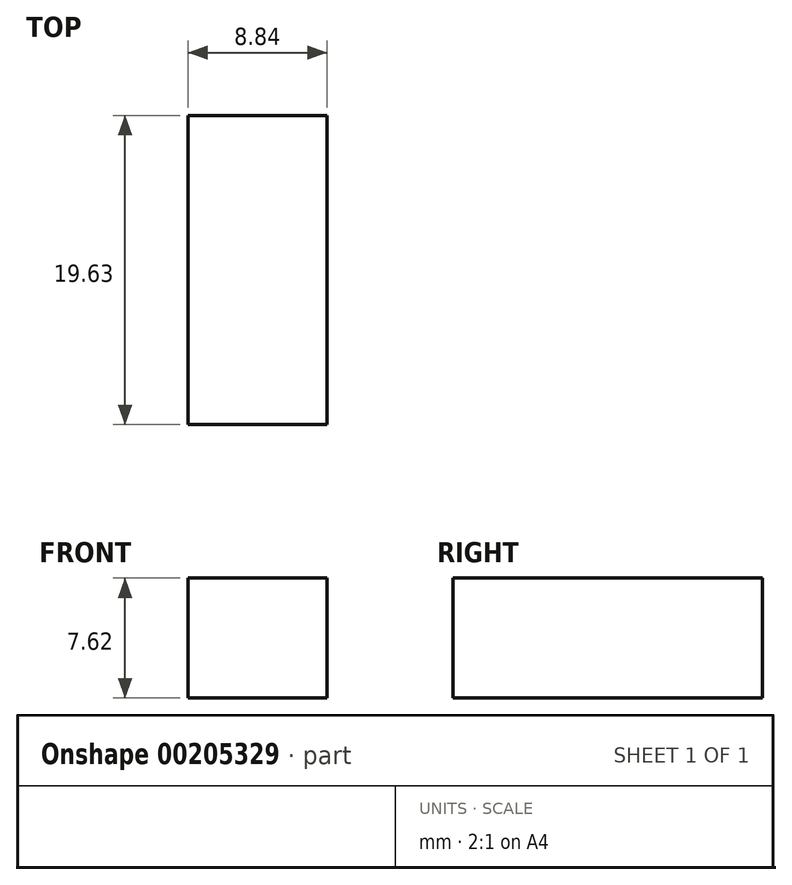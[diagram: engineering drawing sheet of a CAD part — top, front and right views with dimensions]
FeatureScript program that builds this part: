
annotation { "Feature Type Name" : "Feature", "Feature Type Description" : "" }
export const myFeature = defineFeature(function(context is Context, id is Id, definition is map)
    precondition{}
    {
        {
            var Q0;
            Q0=qCreatedBy(makeId("Top.planeOp"),FACE);
            var sketch = newSketch(context, id + "F0", { "sketchPlane" : qUnion([Q0])});
            skLineSegment(sketch, "E0.bottom", {"start": v(-60.42, 23.61) * mm, "end": v(52.56, 23.61) * mm});
            skLineSegment(sketch, "E0.top", {"start": v(-60.42, -27.19) * mm, "end": v(52.56, -27.19) * mm});
            skLineSegment(sketch, "E0.left", {"start": v(-60.42, 23.61) * mm, "end": v(-60.42, -27.19) * mm});
            skLineSegment(sketch, "E0.right", {"start": v(52.56, 23.61) * mm, "end": v(52.56, -27.19) * mm});
            skSolve(sketch);
        }
        {
            var Q0;
            Q0=makeQuery(id+"F0.imprint","IMPRINT",FACE,{"disambiguationData":[TD([[makeQuery(id+"F0.imprint","IMPRINT",EDGE,{"derivedFrom":sQuery(id+"F0.wireOp",EDGE,"E0.bottom")}),-1.0]])]});
            extrude(context, id + "F1", {"entities" : qUnion([Q0]), "oppositeDirection" : true, "depth" : 7.62 * mm});
        }
        {
            var Q0;
            Q0=makeQuery(id+"F1.opExtrude","CAP_FACE",FACE,{"disambiguationData":[OSD([sQuery(id+"F0.wireOp",EDGE,"E0.bottom"),sQuery(id+"F0.wireOp",EDGE,"E0.top"),sQuery(id+"F0.wireOp",EDGE,"E0.left"),sQuery(id+"F0.wireOp",EDGE,"E0.right")])],"isStart":true});
            var sketch = newSketch(context, id + "F2", { "sketchPlane" : qUnion([Q0])});
            skLineSegment(sketch, "E1.bottom", {"start": v(-4.56, -7.56) * mm, "end": v(4.28, -7.56) * mm});
            skLineSegment(sketch, "E1.top", {"start": v(-4.56, -27.19) * mm, "end": v(4.28, -27.19) * mm});
            skLineSegment(sketch, "E1.left", {"start": v(-4.56, -7.56) * mm, "end": v(-4.56, -27.19) * mm});
            skLineSegment(sketch, "E1.right", {"start": v(4.28, -7.56) * mm, "end": v(4.28, -27.19) * mm});
            skSolve(sketch);
        }
        {
            var Q0;
            Q0=makeQuery(id+"F2.imprint","IMPRINT",FACE,{"disambiguationData":[TD([[makeQuery(id+"F2.imprint","IMPRINT",EDGE,{"derivedFrom":sQuery(id+"F2.wireOp",EDGE,"E1.bottom")}),1.0]])]});
            var Q1;
            Q1=sQuery(id+"F2.wireOp",EDGE,"E1.top");
            var Q2;
            Q2=sQuery(id+"F2.wireOp",EDGE,"E1.left");
            var Q3;
            Q3=sQuery(id+"F2.wireOp",EDGE,"E1.bottom");
            var Q4;
            Q4=sQuery(id+"F2.wireOp",EDGE,"E1.right");
            extrude(context, id + "F3", {"entities" : qUnion([Q0]), "operationType" : NewBodyOperationType.REMOVE, "surfaceEntities" : qUnion([Q1, Q2, Q3, Q4]), "oppositeDirection" : true, "depth" : 25.4 * mm});
        }
    });
